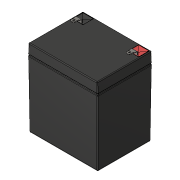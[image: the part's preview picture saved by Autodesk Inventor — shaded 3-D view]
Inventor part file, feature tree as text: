
AUTODESK INVENTOR PART (.ipt)
format: ipt  version: 2020.2 (Build 242310000, 310)  size: 1,527,808 bytes
history: native  units: mm
features: sketch x6, other x4, extrude x3, split x2, surface_op x2, mirror x2, plane x1, thicken_offset x1, sweep x1, fillet x1, projected_geometry x1
ambient origin geometry x8: Origin, YZ Plane, XZ Plane, XY Plane, X Axis, Y Axis, Z Axis, Center Point
bodies: Solid1 (feature_tree), Solid4 (feature_tree)
feature tree (24):
  sketch  "Sketch1"  dims[d0=2.0mm d1=88.6mm]
  sketch  "Sketch2"  dims[d3=90.2mm d4=1.0mm]
  other  "Center"
  extrude  "Extrusion1"  Depth=88.6mm
  extrude  "Extrusion2"  Depth=1.0mm
  split  "Split1"
  split  "Split2"
  plane  "Work Plane1"
  sketch  "Sketch3"  dims[d5=88.8mm d6=101.2mm d7=1.6mm]
  sketch  "Sketch4"  dims[d8=13.2mm d9=1.0mm]
  surface_op  "Trim1"
  surface_op  "Trim2"
  thicken_offset  "Thicken1"
  sweep  "Sweep1"
  mirror  "Mirror1"
  mirror  "Mirror2"
  fillet  "Fillet1"  Radius=1.6mm
  other  "Decal1"
  projected_geometry  "Projected Loop1"
  other  "Srf1"
  sketch  "Sketch5"  dims[d10=2.0mm]
  sketch  "Sketch6"  dims[d11=68.6mm d13=70.3mm d14=70.3mm d15=0.0mm d16=90.2mm d17=0.0mm d18=1.6mm d19=36.0mm d20=13.5mm d21=1.4mm d22=1.6mm d23=4.8mm d24=4.0mm d25=9.0mm d26=1.0mm d27=3.5mm d28=6.6mm d29=0.0mm d30=4.76mm d31=2.9mm d32=1.0mm d33=6.3mm d34=2.53mm d35=1.54mm d36=1.85mm d37=0.8mm d38=0.8mm d39=13.5mm d40=0.5mm d41=0.0mm d42=0.0mm d44=1.0mm d56=50.6mm]
  other  "Image1"
  extrude  "ExtrusionSrf1"  Depth=1.0mm
